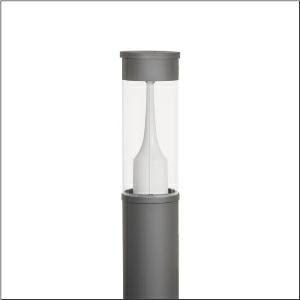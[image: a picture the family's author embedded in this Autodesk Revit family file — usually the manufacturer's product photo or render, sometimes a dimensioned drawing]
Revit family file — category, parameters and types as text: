
# Revit family: city-light_260_iq___p1_0a_5xa5295nf14h_1e18
name_source: partatom
category: Lighting Fixtures
units: mm (PartAtom-declared; Revit-internal decimal feet)

## family parameters
Cut with Voids When Loaded = No
Host = Face
Light Source = No
Part Type = Normal
Room Calculation Point = No
Round Connector Dimension = Use Diameter
Shared = No

## types (1)
- --- (1 x LED, 1510 lm, 11.8 W, 2700K)
    Apparent Load = 12 VA
    CIE Flux Codes = 32 61 90 93 100
    Color Rendering = 70
    Color Temperature = 2700K
    Default Elevation = 1800 mm
    Description = City-Light 260 iQ, light pillar, Module 540 iQ-SR, primary light control with 3 zone facetted reflector, of plastic, silver coated, highly specular, structured, primary optical cover: cover, of PMMA, transparent, partly coated, light distribution: P1.0a, primary light characteristic: strongly asymmetric, LED, High Power LED, rated luminous flux: 1.510lm, luminous efficacy: 128lm/W, light colour: 727, colour temperature: 2700K, control gear: ECG iQ, control: presetting dimming logarithmic, Street-Remote, Auto-Match, Temp-Guard, Lumen-Switch, Night-Set, Smart-Wire, Light-Fading, Desk-Remote (wireless, voltage-free reading and setting of iQ features in the workshop via application-optimized NFC function/RFID function), optimised constant luminous flux control (CLO 2.0), with terminal, 6-pole, max. 2.5mm², mains connection: 230..240V, AC, 50/60Hz, start of lifetime: 12W, end of service life: 12W, reduction: 6W, luminaire housing, cylindrical, of extruded aluminium section, coated, Siteco® metallic grey (DB 702S), length: 2.600mm, diameter: 200mm, Module 540 iQ-SR, traffic white (RAL 9016), equipment: standard, protection rating (complete): IP65, insulation class (complete): insulation class II (safety insulation), certification: CE, ENEC, VDE, packaging unit: 1 piece

Light Distribution: P1.0a
    Height = 500 mm
    Lamp = 1 x LED
    Lamp Light Flux = 1510 lm
    Lamp Power = 11.8 W
    Lamp count = 1
    Length = 200 mm  [stored 0.656168 ft]
    Luminous efficacy = 128 lm/W
    Manufacturer = Siteco
    ModVariant = No
    Model = 5XA5295NF14H
    Mounting Place = Floor
    Mounting Type = Freestanding
    Number of Poles = 1
    OnlyDefault = Yes
    Power Factor = 1
    Product Name = City-Light 260 iQ | P1.0a
    Product group = light pillar
    ProductGroupID = 1303
    Protection Class = Protection class II
    Protection Degree = IP 65
    RLX_Detail_Level = 1
    RLX_Emergency_Light_Flux = 0 lm
    RLX_Emergency_Type = 0
    RLX_Emergency_Type_DB = No
    RlxData = <blob elided: 52549 chars, md5=47660b95>
    Socket = socket
    Standby Power = 0 W
    System Light Flux = 1510 lm
    System Power = 12 W
    Type Comments = factory setting: luminous flux: 100 % | dim-lin: 254 | 472 mA
    Type Image = l_1006918.jpg
    URL = http://relux.com
    VarID = @adj_103307
    Voltage = 0 V
    Weight = 0.00 kg
    Width = 0 mm  [stored 0 ft]

note: [stored X ft] marks values corroborated as IEEE doubles in the binary element streams (Revit-internal decimal feet)

## geometry (parser evidence)
native form markers: Blend x4, Sweep x11
no freeform markers — native parametric forms only
